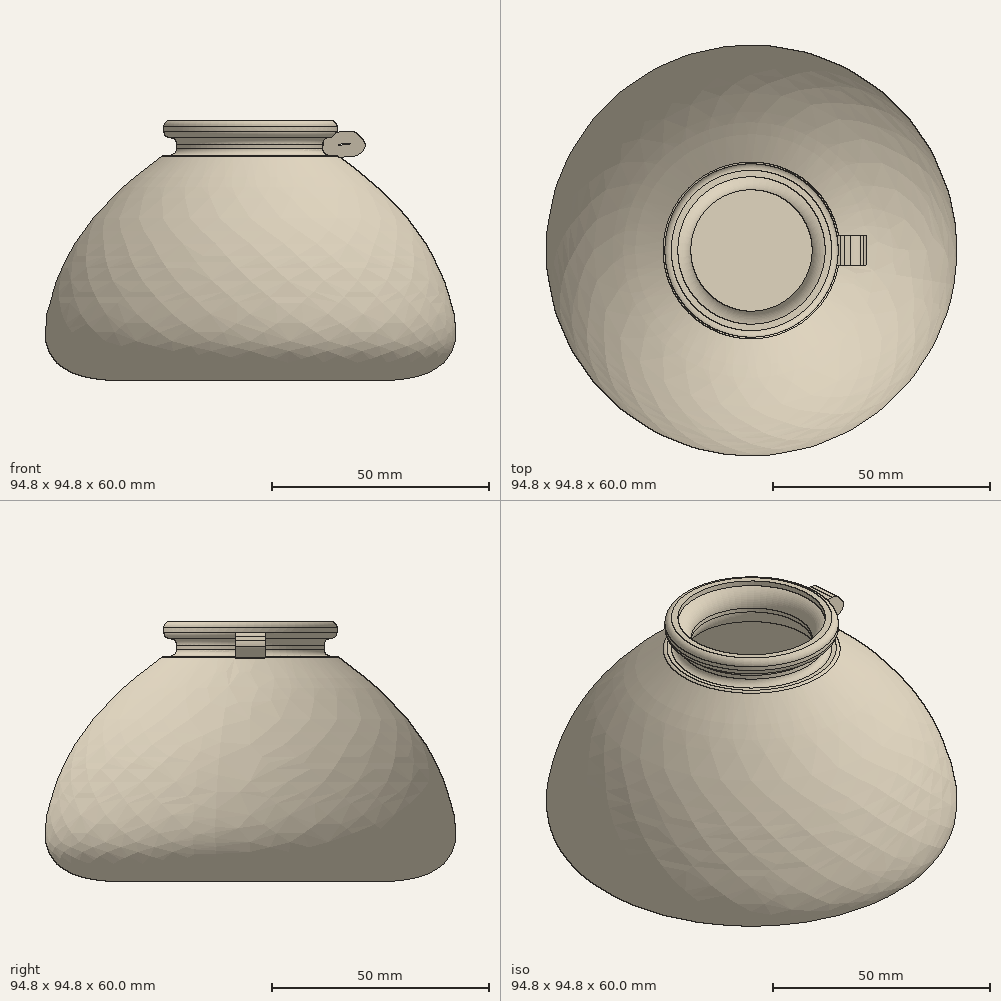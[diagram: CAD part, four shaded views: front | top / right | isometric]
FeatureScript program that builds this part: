
annotation { "Feature Type Name" : "Feature", "Feature Type Description" : "" }
export const myFeature = defineFeature(function(context is Context, id is Id, definition is map)
    precondition{}
    {
        {
            var Q0;
            Q0=qCreatedBy(makeId("Front.planeOp"),FACE);
            var sketch = newSketch(context, id + "F0", { "sketchPlane" : qUnion([Q0])});
            skLineSegment(sketch, "E0", {"start": v(30, 0) * mm, "end": v(0, 0) * mm});
            skLineSegment(sketch, "E1", {"start": v(0, 0) * mm, "end": v(0, 60) * mm});
            skLineSegment(sketch, "E2", {"start": v(0, 60) * mm, "end": v(20, 60) * mm});
            skLineSegment(sketch, "E3", {"start": v(20, 60) * mm, "end": v(20, 56) * mm});
            skLineSegment(sketch, "E4", {"start": v(20, 56) * mm, "end": v(17, 56) * mm});
            skLineSegment(sketch, "E5", {"start": v(17, 56) * mm, "end": v(17, 52) * mm});
            skLineSegment(sketch, "E6", {"start": v(17, 52) * mm, "end": v(20, 52) * mm});
            skFitSpline(sketch, "E7", {"points": [v(20, 52) * mm, v(46, 19.15) * mm, v(30, 0) * mm], "startDerivative": vector(83.23, -59.6) * mm, "endDerivative": vector(-133.31, 0) * mm});
            skSolve(sketch);
        }
        {
            var Q0;
            Q0 = qSketchRegion(id + "F0", true);
            var Q1;
            Q1=sQuery(id+"F0.wireOp",EDGE,"E1");
            revolve(context, id + "F1", {"surfaceOperationType" : NewSurfaceOperationType.NEW, "entities" : qUnion([Q0]), "axis" : qUnion([Q1]), "revolveType" : RevolveType.FULL});
        }
        {
            var Q0;
            Q0=makeQuery(id+"F1.opRevolve","SWEPT_FACE",FACE,{"disambiguationData":[OSD([sQuery(id+"F0.wireOp",EDGE,"E2")])]});
            var Q1;
            Q1=makeQuery(id+"F1.opRevolve","SWEPT_EDGE",EDGE,{"disambiguationData":[OSD([sQuery(id+"F0.wireOp",EDGE,"E3"),sQuery(id+"F0.wireOp",EDGE,"E4")])]});
            var Q2;
            Q2=makeQuery(id+"F1.opRevolve","SWEPT_EDGE",EDGE,{"disambiguationData":[OSD([sQuery(id+"F0.wireOp",EDGE,"E5"),sQuery(id+"F0.wireOp",EDGE,"E6")])]});
            var Q3;
            Q3=makeQuery(id+"F1.opRevolve","SWEPT_EDGE",EDGE,{"disambiguationData":[OSD([sQuery(id+"F0.wireOp",EDGE,"E6"),sQuery(id+"F0.wireOp",EDGE,"E7")])]});
            var Q4;
            Q4=makeQuery(id+"F1.opRevolve","SWEPT_EDGE",EDGE,{"disambiguationData":[OSD([sQuery(id+"F0.wireOp",EDGE,"E4"),sQuery(id+"F0.wireOp",EDGE,"E5")])]});
            fillet(context, id + "F2", {"entities" : qUnion([Q0, Q1, Q2, Q3, Q4]), "radius" : 1.5 * mm, "tangentPropagation" : true, "allowEdgeOverflow" : false});
        }
        {
            var Q0;
            Q0=makeQuery(id+"F1.opRevolve","SWEPT_FACE",FACE,{"disambiguationData":[OSD([sQuery(id+"F0.wireOp",EDGE,"E2")])]});
            shell(context, id + "F3", {"entities" : qUnion([Q0]), "thickness" : 3 * mm});
        }
        {
            var Q0;
            Q0=qCreatedBy(makeId("Front.planeOp"),FACE);
            var sketch = newSketch(context, id + "F4", { "sketchPlane" : qUnion([Q0])});
            skLineSegment(sketch, "E8", {"start": v(16, 56) * mm, "end": v(21, 57.5) * mm});
            skLineSegment(sketch, "E9", {"start": v(21, 57.5) * mm, "end": v(24.32, 57.5) * mm});
            skLineSegment(sketch, "E10", {"start": v(24.32, 57.5) * mm, "end": v(26.57, 54.82) * mm});
            skLineSegment(sketch, "E11", {"start": v(26.57, 54.82) * mm, "end": v(26.57, 52) * mm});
            skLineSegment(sketch, "E12", {"start": v(26.57, 52) * mm, "end": v(18.6, 51.3) * mm});
            skLineSegment(sketch, "E13", {"start": v(18.6, 51.3) * mm, "end": v(16, 52) * mm});
            skLineSegment(sketch, "E14", {"start": v(16, 52) * mm, "end": v(16, 56) * mm});
            skSolve(sketch);
        }
        {
            var Q0;
            Q0 = qSketchRegion(id + "F4", true);
            extrude(context, id + "F5", {"entities" : qUnion([Q0]), "operationType" : NewBodyOperationType.ADD, "endBound" : BoundingType.SYMMETRIC, "depth" : 7 * mm, "offsetDistance" : 25 * mm});
        }
        {
            var Q0;
            Q0=makeQuery(id+"F5.opExtrude","SWEPT_EDGE",EDGE,{"disambiguationData":[OSD([sQuery(id+"F4.wireOp",EDGE,"E8"),sQuery(id+"F4.wireOp",EDGE,"E9")])]});
            var Q1;
            Q1=makeQuery(id+"F5.opExtrude","SWEPT_EDGE",EDGE,{"disambiguationData":[OSD([sQuery(id+"F4.wireOp",EDGE,"E9"),sQuery(id+"F4.wireOp",EDGE,"E10")])]});
            var Q2;
            Q2=makeQuery(id+"F5.opExtrude","SWEPT_EDGE",EDGE,{"disambiguationData":[OSD([sQuery(id+"F4.wireOp",EDGE,"E10"),sQuery(id+"F4.wireOp",EDGE,"E11")])]});
            var Q3;
            Q3=makeQuery(id+"F5.opExtrude","SWEPT_EDGE",EDGE,{"disambiguationData":[OSD([sQuery(id+"F4.wireOp",EDGE,"E11"),sQuery(id+"F4.wireOp",EDGE,"E12")])]});
            fillet(context, id + "F6", {"entities" : qUnion([Q0, Q1, Q2, Q3]), "radius" : 3 * mm, "tangentPropagation" : true, "allowEdgeOverflow" : false});
        }
        {
            var Q0;
            Q0=makeQuery(id+"F5.opExtrude","CAP_FACE",FACE,{"disambiguationData":[OSD([sQuery(id+"F4.wireOp",EDGE,"E8"),sQuery(id+"F4.wireOp",EDGE,"E9"),sQuery(id+"F4.wireOp",EDGE,"E10"),sQuery(id+"F4.wireOp",EDGE,"E11"),sQuery(id+"F4.wireOp",EDGE,"E12"),sQuery(id+"F4.wireOp",EDGE,"E13"),sQuery(id+"F4.wireOp",EDGE,"E14")])],"isStart":false});
            var Q1;
            Q1=makeQuery(id+"F5.opExtrude","CAP_FACE",FACE,{"disambiguationData":[OSD([sQuery(id+"F4.wireOp",EDGE,"E8"),sQuery(id+"F4.wireOp",EDGE,"E9"),sQuery(id+"F4.wireOp",EDGE,"E10"),sQuery(id+"F4.wireOp",EDGE,"E11"),sQuery(id+"F4.wireOp",EDGE,"E12"),sQuery(id+"F4.wireOp",EDGE,"E13"),sQuery(id+"F4.wireOp",EDGE,"E14")])],"isStart":true});
            shell(context, id + "F7", {"entities" : qUnion([Q0, Q1]), "thickness" : 2.8 * mm});
        }
    });
